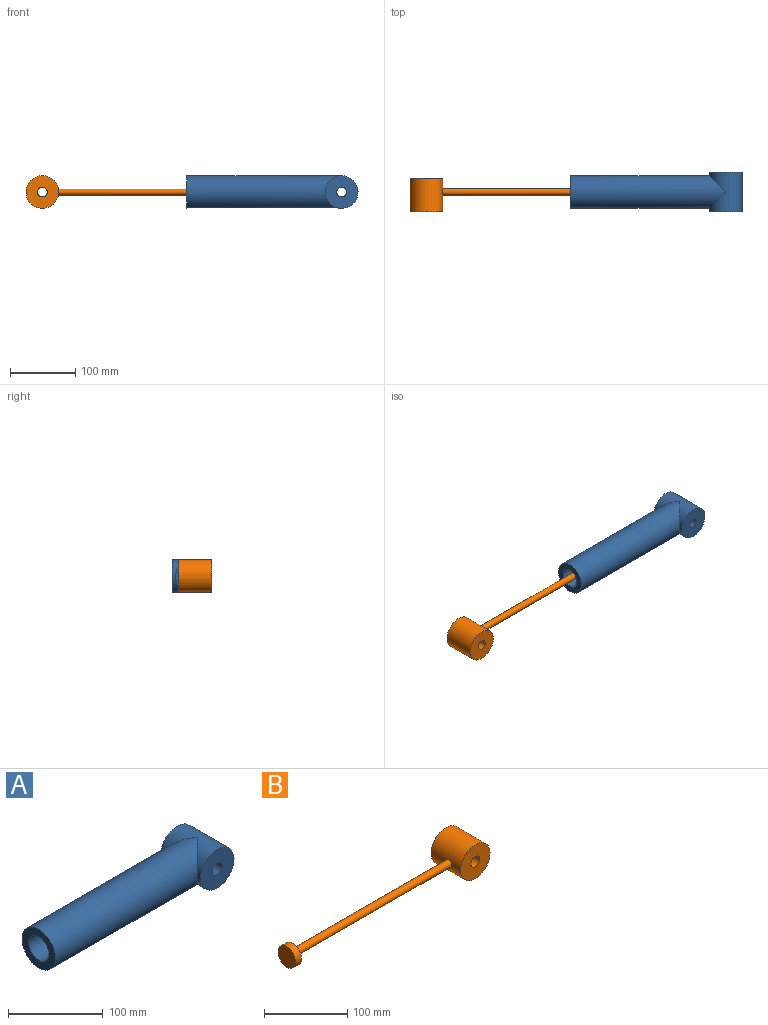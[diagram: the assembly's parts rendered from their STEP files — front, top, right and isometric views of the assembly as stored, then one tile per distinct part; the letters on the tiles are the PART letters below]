
ASSEMBLY  parts=2 mates=1
PART A: 10 faces, bbox 262x60x50 mm
  f0: cylinder r=25mm len=236.99mm, axis (-1,0,0), area 34727mm2, adj f1,f4
  f1: plane 50x50mm, normal (-1,0,0), area 1256.6mm2, adj f0,f2
  f2: cylinder r=15mm len=200mm, axis (-1,0,0), area 18849.6mm2, adj f1,f3
  f3: plane 30x30mm, normal (-1,0,0), area 706.9mm2, adj f2
  f4: cylinder r=25mm len=60mm, axis (0,1,0), area 6924.7mm2, adj f0,f5,f6,f7,f8
  f5: plane 50x50mm, normal (0,-1,0), area 1786.8mm2, adj f4,f9
  f6: plane 50x50mm, normal (0,1,0), area 1786.8mm2, adj f4,f9
  f7: cylinder r=25mm len=0.43mm, axis (-1,0,0), area 0mm2, adj f4
  f8: cylinder r=25mm len=0.43mm, axis (-1,0,0), area 0mm2, adj f4
  f9: cylinder r=7.5mm len=60mm, axis (0,-1,0), area 2827.4mm2, adj f5,f6
PART B: 8 faces, bbox 325.1x50x50 mm
  f0: cylinder r=5mm len=265.56mm, axis (1,0,0), area 8334.8mm2, adj f2,f4
  f1: plane 30x30mm, normal (-1,0,0), area 706.9mm2, adj f3
  f2: plane 30x30mm, normal (1,0,0), area 628.3mm2, adj f0,f3
  f3: cylinder r=15mm len=30mm, axis (1,0,0), area 942.5mm2, adj f1,f2
  f4: cylinder r=25mm len=50mm, axis (0,1,0), area 7774.9mm2, adj f0,f5,f6
  f5: plane 50x50mm, normal (0,-1,0), area 1786.8mm2, adj f4,f7
  f6: plane 50x50mm, normal (0,1,0), area 1786.8mm2, adj f4,f7
  f7: cylinder r=7.5mm len=50mm, axis (0,-1,0), area 2356.2mm2, adj f5,f6
PLACE A rot(axis=(0,0,1),0deg) t=(77.57,-116.07,190.62)mm fixed
PLACE B rot(axis=(0,0,-1),180deg) t=(-63.24,-116.07,190.62)mm
MATE slider B.f0 <-> A.f0  axis (1,0,0) through (38.25,-116.07,190.62)mm
